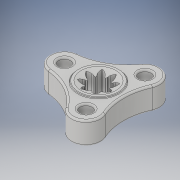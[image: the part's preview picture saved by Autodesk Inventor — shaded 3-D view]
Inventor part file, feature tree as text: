
AUTODESK INVENTOR PART (.ipt)
format: ipt  version: 2017 (Build 210142000, 142)  size: 525,824 bytes
history: native  units: in
note: dims shown in document units (in); Inventor stores cm internally (conversion verified against a paired STEP export)
features: extrude x6, sketch x6, fillet x2, revolve x1
ambient origin geometry x8: Origin, YZ Plane, XZ Plane, XY Plane, X Axis, Y Axis, Z Axis, Center Point
bodies: Solid1 (feature_tree)
feature tree (15):
  extrude  "Extrusion9"  Depth=0.005in
  extrude  "Extrusion11"  TaperAngle=22.5deg  [1 undecoded]
  revolve  "Revolution1"  [1 undecoded]
  extrude  "Extrusion12"  Depth=0.01in TaperAngle=0.0deg
  extrude  "Extrusion13"  Depth=0.01in
  fillet  "Fillet6"  Radius=0.01in
  extrude  "Extrusion14"  Depth=0.15in
  extrude  "Extrusion15"  Depth=0.015in
  fillet  "Fillet7"  Radius=0.587in
  sketch  "Sketch12"  dims[d41=0.215in d42=0.0in d100=0.005in]
  sketch  "Sketch13"  dims[d101=1.0in d102=0.0in d106=22.5deg]
  sketch  "Sketch14"  dims[d107=90.0deg d110=0.35in]
  sketch  "Sketch15"  dims[d111=1.0in d112=0.01in d113=0.0in]
  sketch  "Sketch16"  dims[d114=0.35in d115=1.0in d116=0.01in d117=0.0in]
  sketch  "Sketch17"  dims[d118=0.005in d119=0.15in d120=0.865in d121=0.587in d122=1.1811in d124=360.0deg d126=0.105in d127=1.0in d128=0.0in d129=0.25in d130=0.25in d131=0.25in d132=0.5in d133=0.5in d134=0.5in d135=1.0in d136=0.0in d137=0.0in d138=0.015in]
note: 2 required parameter values undecoded (feature->parameter linkage not recoverable at this tier; creation-order binding heuristic only, values carry confidence <= 0.55)